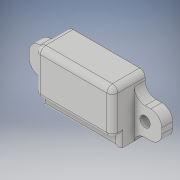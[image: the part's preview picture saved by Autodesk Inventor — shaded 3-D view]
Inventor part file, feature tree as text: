
AUTODESK INVENTOR PART (.ipt)
format: ipt  version: 2018 (Build 220112000, 112)  size: 215,552 bytes
history: native  units: in
note: dims shown in document units (in); Inventor stores cm internally (conversion verified against a paired STEP export)
features: fillet x7, extrude x5, sketch x5, shell x1, chamfer x1
ambient origin geometry x8: Origin, YZ Plane, XZ Plane, XY Plane, X Axis, Y Axis, Z Axis, Center Point
bodies: Solid1 (feature_tree)
feature tree (19):
  extrude  "Extrusion1"  Depth=0.6496in
  shell  "Shell1"  Thickness=0.2559in
  extrude  "Extrusion2"  TaperAngle=0.0deg  [1 undecoded]
  fillet  "Fillet1"  Radius=0.315in
  fillet  "Fillet2"  Radius=0.315in
  extrude  "Extrusion3"  Depth=0.125in
  extrude  "Extrusion4"  Depth=0.1181in
  chamfer  "Chamfer1"  Distance=0.25in
  fillet  "Fillet4"  Radius=0.2362in
  extrude  "Extrusion5"  Depth=0.125in
  fillet  "Fillet5"  Radius=0.0787in
  fillet  "Fillet6"  Radius=0.0625in
  fillet  "Fillet7"  Radius=0.315in
  fillet  "Fillet8"  Radius=0.315in
  sketch  "Sketch1"  dims[d0=0.5118in d1=0.6496in d2=0.2559in d3=0.0in]
  sketch  "Sketch2"  dims[d4=0.1181in d5=0.0in d7=0.315in d8=0.315in]
  sketch  "Sketch3"  dims[d10=0.125in d11=0.0in d12=0.125in]
  sketch  "Sketch4"  dims[d13=0.125in d14=0.1181in]
  sketch  "Sketch5"  dims[d15=0.1181in d16=0.25in d17=0.0in d18=0.2362in d19=0.2362in d20=0.0787in d21=0.0in d23=0.0625in d25=0.315in d26=0.315in d27=0.0787in d28=0.125in d29=45.0deg d30=0.1378in d31=0.0787in d32=0.0in d33=0.0394in d34=0.0394in d35=0.0787in d36=0.125in]
note: 1 required parameter value undecoded (feature->parameter linkage not recoverable at this tier; creation-order binding heuristic only, values carry confidence <= 0.55)
